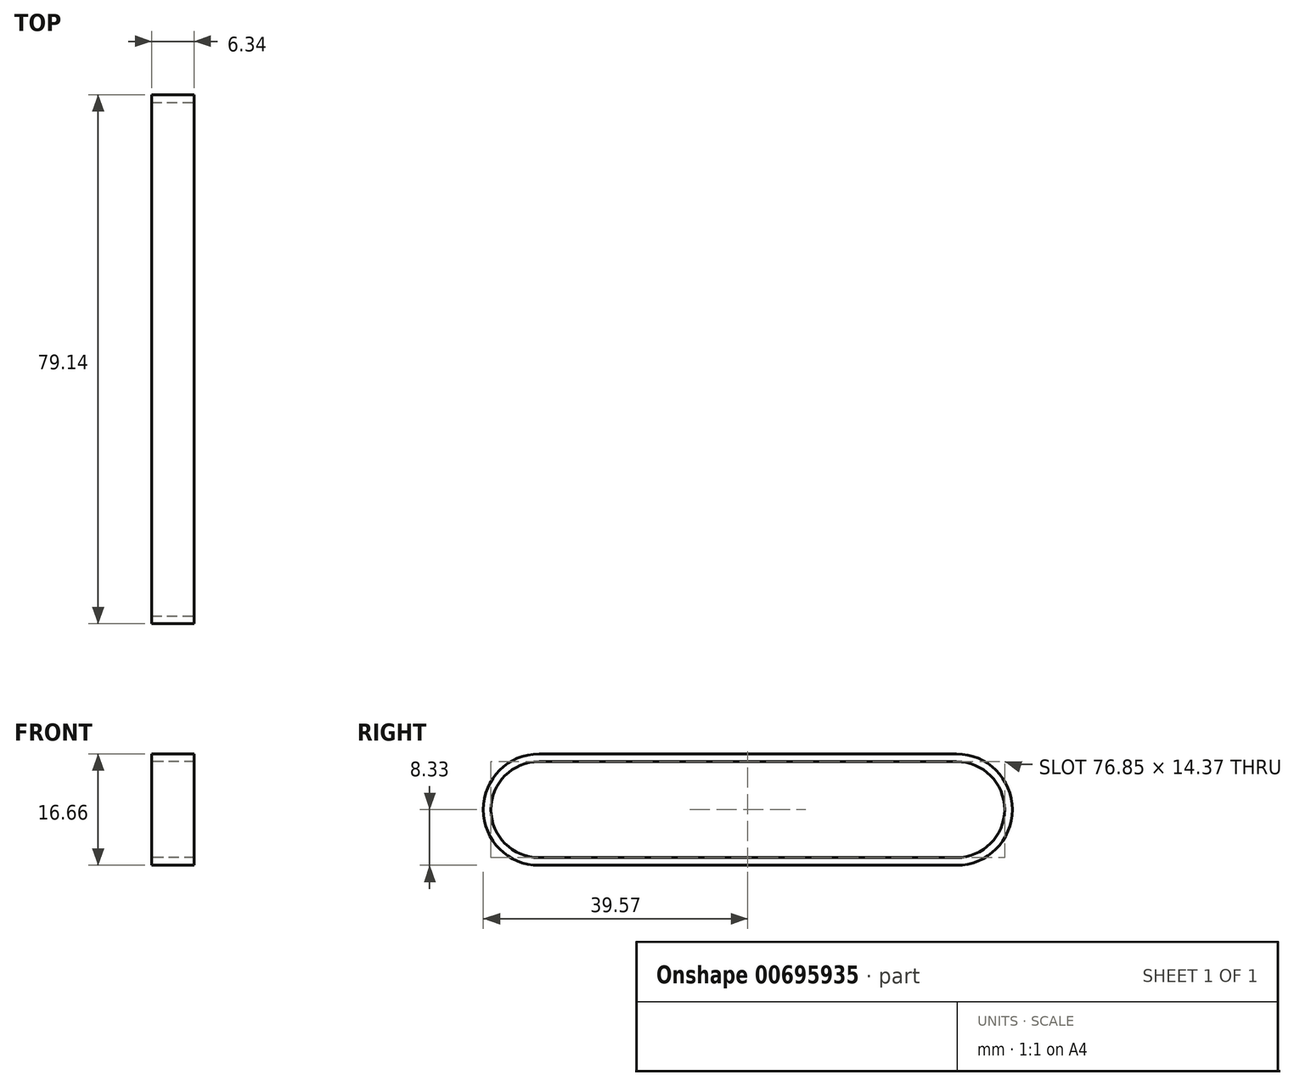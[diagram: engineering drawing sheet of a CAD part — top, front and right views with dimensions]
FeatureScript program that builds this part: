
annotation { "Feature Type Name" : "Feature", "Feature Type Description" : "" }
export const myFeature = defineFeature(function(context is Context, id is Id, definition is map)
    precondition{}
    {
        {
            var Q0;
            Q0=qCreatedBy(makeId("Right.planeOp"),FACE);
            var sketch = newSketch(context, id + "F0", { "sketchPlane" : qUnion([Q0])});
            skLineSegment(sketch, "E0", {"start": v(-31.24, 7.76) * mm, "end": v(31.24, 7.76) * mm});
            skLineSegment(sketch, "E1", {"start": v(-31.24, -7.76) * mm, "end": v(31.24, -7.76) * mm});
            skArc(sketch, "E2", {"start": v(-31.24, 7.76) * mm, "mid": v(-39, 0) * mm, "end": v(-31.24, -7.76) * mm});
            skArc(sketch, "E3", {"start": v(31.24, -7.76) * mm, "mid": v(39, 0) * mm, "end": v(31.24, 7.76) * mm});
            skLineSegment(sketch, "E4", {"start": v(-31.24, 0) * mm, "end": v(31.24, 0) * mm, "construction": true});
            skSolve(sketch);
        }
        {
            var Q0;
            Q0=qCreatedBy(makeId("Front.planeOp"),FACE);
            var sketch = newSketch(context, id + "F1", { "sketchPlane" : qUnion([Q0])});
            skLineSegment(sketch, "E5.bottom", {"start": v(3.18, 7.18) * mm, "end": v(-3.18, 7.18) * mm});
            skLineSegment(sketch, "E5.top", {"start": v(3.18, 8.33) * mm, "end": v(-3.18, 8.33) * mm});
            skLineSegment(sketch, "E5.left", {"start": v(3.18, 7.18) * mm, "end": v(3.18, 8.33) * mm});
            skLineSegment(sketch, "E5.right", {"start": v(-3.18, 7.18) * mm, "end": v(-3.18, 8.33) * mm});
            skPoint(sketch, "E5.middle", {"position": v(0, 7.76) * mm});
            skSolve(sketch);
        }
        {
            var Q0;
            Q0=makeQuery(id+"F1.imprint","IMPRINT",FACE,{"disambiguationData":[TD([[makeQuery(id+"F1.imprint","IMPRINT",EDGE,{"derivedFrom":sQuery(id+"F1.wireOp",EDGE,"E5.bottom")}),-1.0]])]});
            var Q1;
            Q1=sQuery(id+"F0.wireOp",EDGE,"E3");
            var Q2;
            Q2=sQuery(id+"F0.wireOp",EDGE,"E0");
            var Q3;
            Q3=sQuery(id+"F0.wireOp",EDGE,"E2");
            var Q4;
            Q4=sQuery(id+"F0.wireOp",EDGE,"E1");
            sweep(context, id + "F2", {"profiles" : qUnion([Q0]), "path" : qUnion([Q1, Q2, Q3, Q4])});
        }
    });
